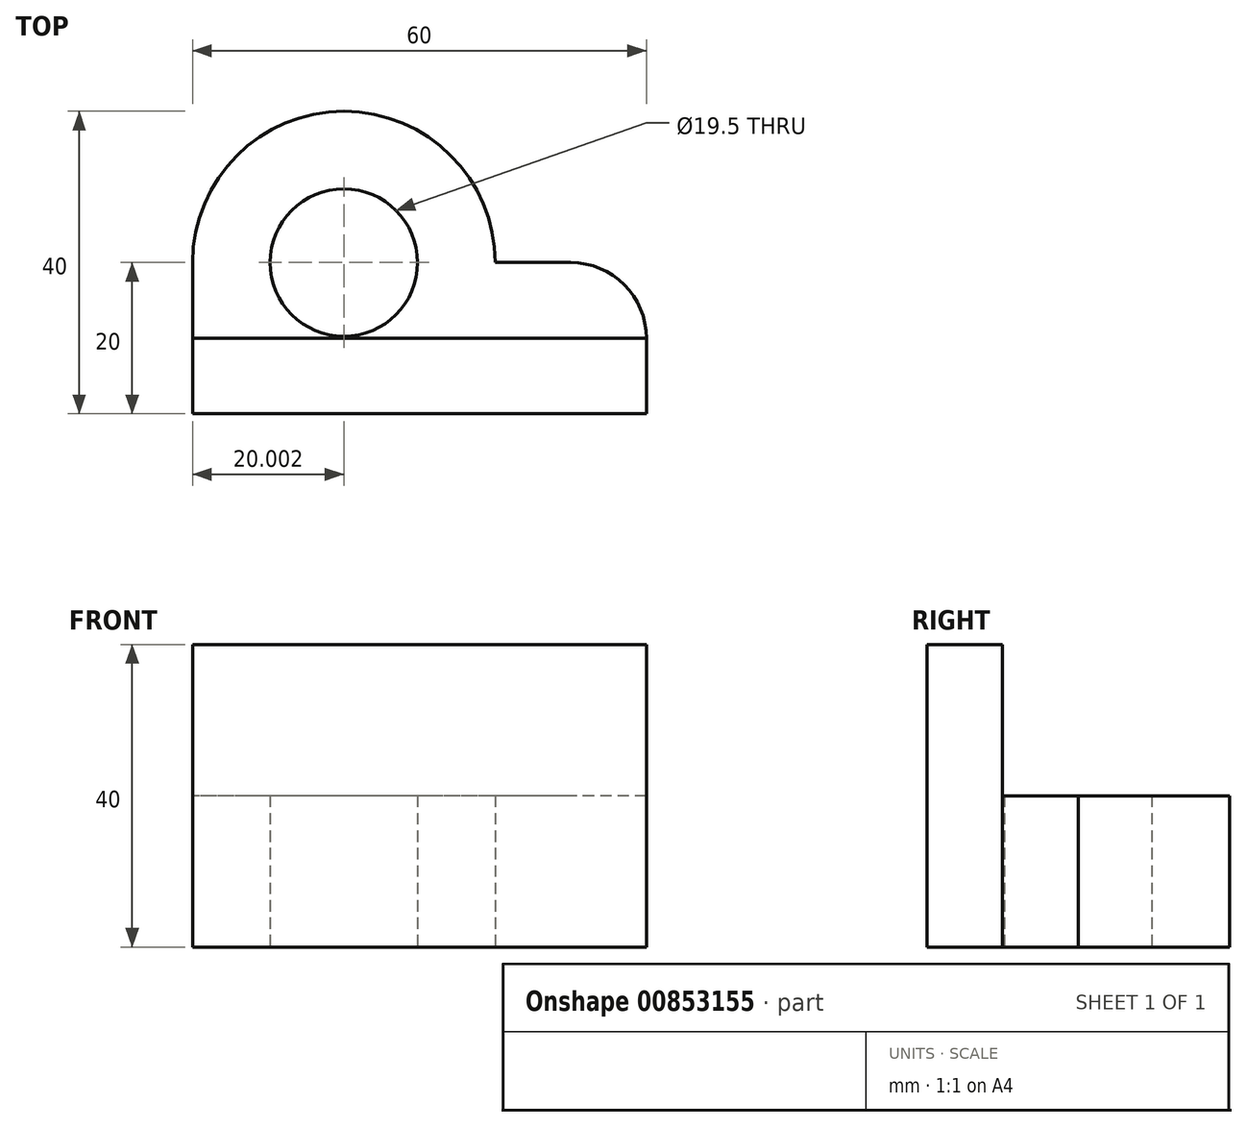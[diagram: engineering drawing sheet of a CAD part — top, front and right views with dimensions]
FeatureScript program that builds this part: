
annotation { "Feature Type Name" : "Feature", "Feature Type Description" : "" }
export const myFeature = defineFeature(function(context is Context, id is Id, definition is map)
    precondition{}
    {
        {
            var Q0;
            Q0=qCreatedBy(makeId("Top.planeOp"),FACE);
            var sketch = newSketch(context, id + "F0", { "sketchPlane" : qUnion([Q0])});
            skLineSegment(sketch, "E0", {"start": v(-34.97, 0) * mm, "end": v(25.03, 0) * mm});
            skLineSegment(sketch, "E1", {"start": v(-34.97, 0) * mm, "end": v(-34.97, 10) * mm});
            skLineSegment(sketch, "E2", {"start": v(-34.97, 10) * mm, "end": v(-34.97, 20) * mm});
            skLineSegment(sketch, "E3", {"start": v(25.03, 10) * mm, "end": v(25.03, 10) * mm});
            skLineSegment(sketch, "E4", {"start": v(25.03, 10) * mm, "end": v(-34.97, 10) * mm});
            skPoint(sketch, "E5.visualSharp", {"position": v(25.03, 20) * mm});
            skArc(sketch, "E5.filletArc", {"start": v(25.03, 10) * mm, "mid": v(22.1, 17.07) * mm, "end": v(15.03, 20) * mm});
            skCircle(sketch, "E6", {"center": v(-14.97, 20) * mm, "radius": 9.75 * mm});
            skArc(sketch, "E7", {"start": v(5.03, 20) * mm, "mid": v(-14.97, 40) * mm, "end": v(-34.97, 20) * mm});
            skLineSegment(sketch, "E8", {"start": v(15.03, 20) * mm, "end": v(5.03, 20) * mm});
            skLineSegment(sketch, "E9", {"start": v(25.03, 0) * mm, "end": v(25.03, 10) * mm});
            skSolve(sketch);
        }
        {
            var Q0;
            Q0=makeQuery(id+"F0.imprint","IMPRINT",FACE,{"disambiguationData":[TD([[makeQuery(id+"F0.imprint","IMPRINT",EDGE,{"derivedFrom":sQuery(id+"F0.wireOp",EDGE,"E0")}),1.0]])]});
            extrude(context, id + "F1", {"entities" : qUnion([Q0]), "depth" : 40 * mm, "offsetDistance" : 25 * mm});
        }
        {
            var Q0;
            {var subQ2=sQuery(id+"F0.wireOp",EDGE,"E2");Q0=makeQuery(id+"F0.imprint","IMPRINT",FACE,{"disambiguationData":[TD([[makeQuery(id+"F0.imprint","IMPRINT",EDGE,{"derivedFrom":subQ2}),-1.0]])]});}
            extrude(context, id + "F2", {"entities" : qUnion([Q0]), "depth" : 20 * mm, "offsetDistance" : 25 * mm});
        }
    });
